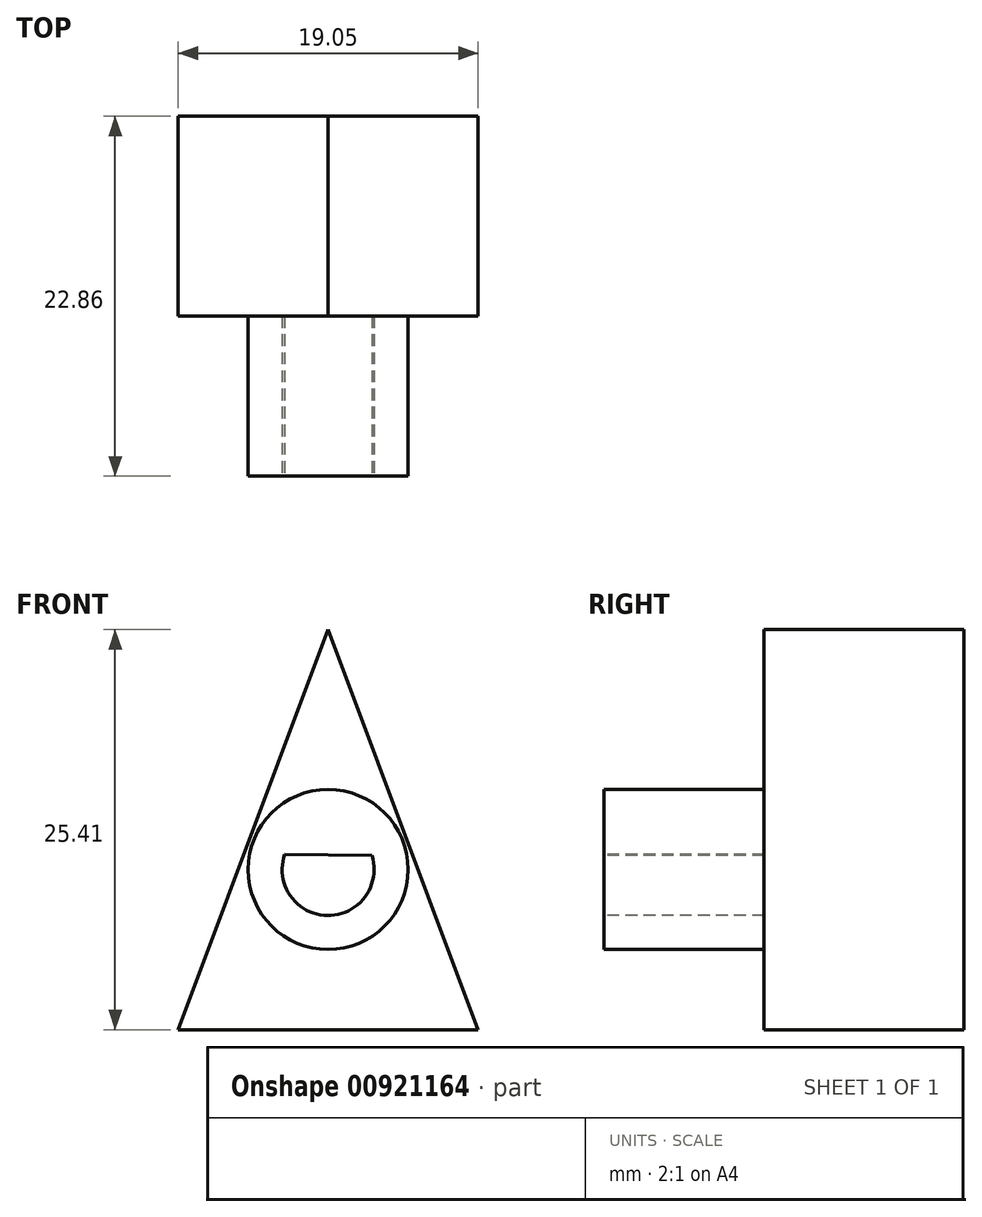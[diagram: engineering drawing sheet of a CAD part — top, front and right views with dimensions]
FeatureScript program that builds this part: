
annotation { "Feature Type Name" : "Feature", "Feature Type Description" : "" }
export const myFeature = defineFeature(function(context is Context, id is Id, definition is map)
    precondition{}
    {
        {
            var Q0;
            Q0=qCreatedBy(makeId("Front.planeOp"),FACE);
            var sketch = newSketch(context, id + "F0", { "sketchPlane" : qUnion([Q0])});
            skLineSegment(sketch, "E0", {"start": v(0, 0) * mm, "end": v(0, 12.81) * mm});
            skLineSegment(sketch, "E1", {"start": v(0, 0) * mm, "end": v(0, -12.59) * mm});
            skLineSegment(sketch, "E2", {"start": v(-9.52, -12.6) * mm, "end": v(9.53, -12.6) * mm});
            skLineSegment(sketch, "E3", {"start": v(0, 12.81) * mm, "end": v(-9.52, -12.6) * mm});
            skLineSegment(sketch, "E4", {"start": v(0, 12.81) * mm, "end": v(9.53, -12.6) * mm});
            skSolve(sketch);
        }
        {
            var Q0;
            Q0 = qSketchRegion(id + "F0", true);
            extrude(context, id + "F1", {"entities" : qUnion([Q0]), "depth" : 12.7 * mm, "offsetDistance" : 25.4 * mm});
        }
        {
            var Q0;
            Q0=makeQuery(id+"F1.opExtrude","CAP_FACE",FACE,{"disambiguationData":[OSD([sQuery(id+"F0.wireOp",EDGE,"E2"),sQuery(id+"F0.wireOp",EDGE,"E3"),sQuery(id+"F0.wireOp",EDGE,"E4")])],"isStart":false});
            var sketch = newSketch(context, id + "F2", { "sketchPlane" : qUnion([Q0])});
            skPoint(sketch, "E5", {"position": v(0, -2.43) * mm});
            skCircle(sketch, "E6", {"center": v(0, -2.43) * mm, "radius": 5.08 * mm});
            skSolve(sketch);
        }
        {
            var Q0;
            Q0 = qSketchRegion(id + "F2", true);
            extrude(context, id + "F3", {"entities" : qUnion([Q0]), "operationType" : NewBodyOperationType.ADD, "depth" : 10.16 * mm, "offsetDistance" : 25.4 * mm});
        }
        {
            var Q0;
            Q0=makeQuery(id+"F3.opExtrude","CAP_FACE",FACE,{"disambiguationData":[OSD([sQuery(id+"F2.wireOp",EDGE,"E6")])],"isStart":false});
            var sketch = newSketch(context, id + "F4", { "sketchPlane" : qUnion([Q0])});
            skCircle(sketch, "E7", {"center": v(0, -2.43) * mm, "radius": 2.92 * mm});
            skLineSegment(sketch, "E8", {"start": v(0, -5.35) * mm, "end": v(0, -1.54) * mm});
            skLineSegment(sketch, "E9", {"start": v(-2.75, -1.45) * mm, "end": v(2.78, -1.54) * mm});
            skSolve(sketch);
        }
        {
            var Q0;
            {var subQ2=sQuery(id+"F4.wireOp",EDGE,"E9");Q0=makeQuery(id+"F4.imprint","IMPRINT",FACE,{"disambiguationData":[TD([[makeQuery(id+"F4.imprint","IMPRINT",EDGE,{"derivedFrom":subQ2}),-1.0]])]});}
            extrude(context, id + "F5", {"entities" : qUnion([Q0]), "operationType" : NewBodyOperationType.REMOVE, "oppositeDirection" : true, "depth" : 10.16 * mm, "offsetDistance" : 25.4 * mm});
        }
    });
